# Revit family: PRD_FrankeWS_SnksSuprts_SiriusBracketForUtilitySinks_BS354
name_source: partatom
category: Plumbing Fixtures
revit_build: Autodesk Revit 2018 (Build: 20190510_1515(x64)
units: mm (PartAtom-declared; Revit-internal decimal feet)

## family parameters
Always vertical = No
Cut with Voids When Loaded = No
OmniClass Number = 23.45.05.00
OmniClass Title = Sanitary Equipment
Part Type = Normal
Room Calculation Point = No
Round Connector Dimension = Use Diameter
Shared = Yes
Work Plane-Based = No

## types (1)
- BS354
    AssetType = Fixed
    BIMObjectName = PRD_AR_SinkSupports_SiriusBracketForUtilitySinks_BS354
    BracketMaterial = PRD_AR_StainlessSteel_SatinFinished
    Category = Pr_20_85_09_88, Sink supports
    Color = Stainless steel
    Description = Bracket for wall mounting, stainless steel, surface satin finished, material thickness 1.5 mm, incl. stainless steel screws and dowels.
    DurationUnit = year
    Features = stainless steel, 1.50 mm, satin finished, wall mounting, 40x320x525 mm (WxHxD)
    Finish = Satin finished
    Form = Wall-mounted
    GrossWeight = 1.70 kg
    IfcExportAs = IfcBuildingElementProxy
    IfcExportType = NOTDEFINED
    Manufacturer = KWC Group AG
    ManufacturerName = KWC Group AG
    ManufacturerURL = www.kwc.com
    Material = Stainless steel
    MaterialThickness = 2 mm  [stored 0.00656168 ft]
    MaterialsBracketsBody = Stainless steel 1.4301
    MaterialsBracketsFinishAndColour = Satin finished
    Model = BS354
    ModelNumber = 2000056824
    ModelReference = BS354
    NBSDescription = Supports for sinks
    NBSReference = 45-35-70/347
    Name = SIRIUS bracket for utility sinks BS354
    NetWeight = 1.40 kg
    NominalHeight = 320 mm  [stored 1.04987 ft]
    NominalLength = 40 mm  [stored 0.131234 ft]
    NominalWidth = 525 mm
    ProductInformation = https://pim.kwc.com
    Shape = Triangular
    Size = 40 x 320 x 525 mm
    URL = www.kwc.com
    Uniclass2015Code = Pr_20_85_09_88
    Uniclass2015Title = Sink supports
    Uniclass2015Version = Products v1.5
    Version = 1
    WarrantyDurationUnit = year

note: [stored X ft] marks values corroborated as IEEE doubles in the binary element streams (Revit-internal decimal feet)

## geometry (parser evidence)
native form markers: Sweep x3
no freeform markers — native parametric forms only
